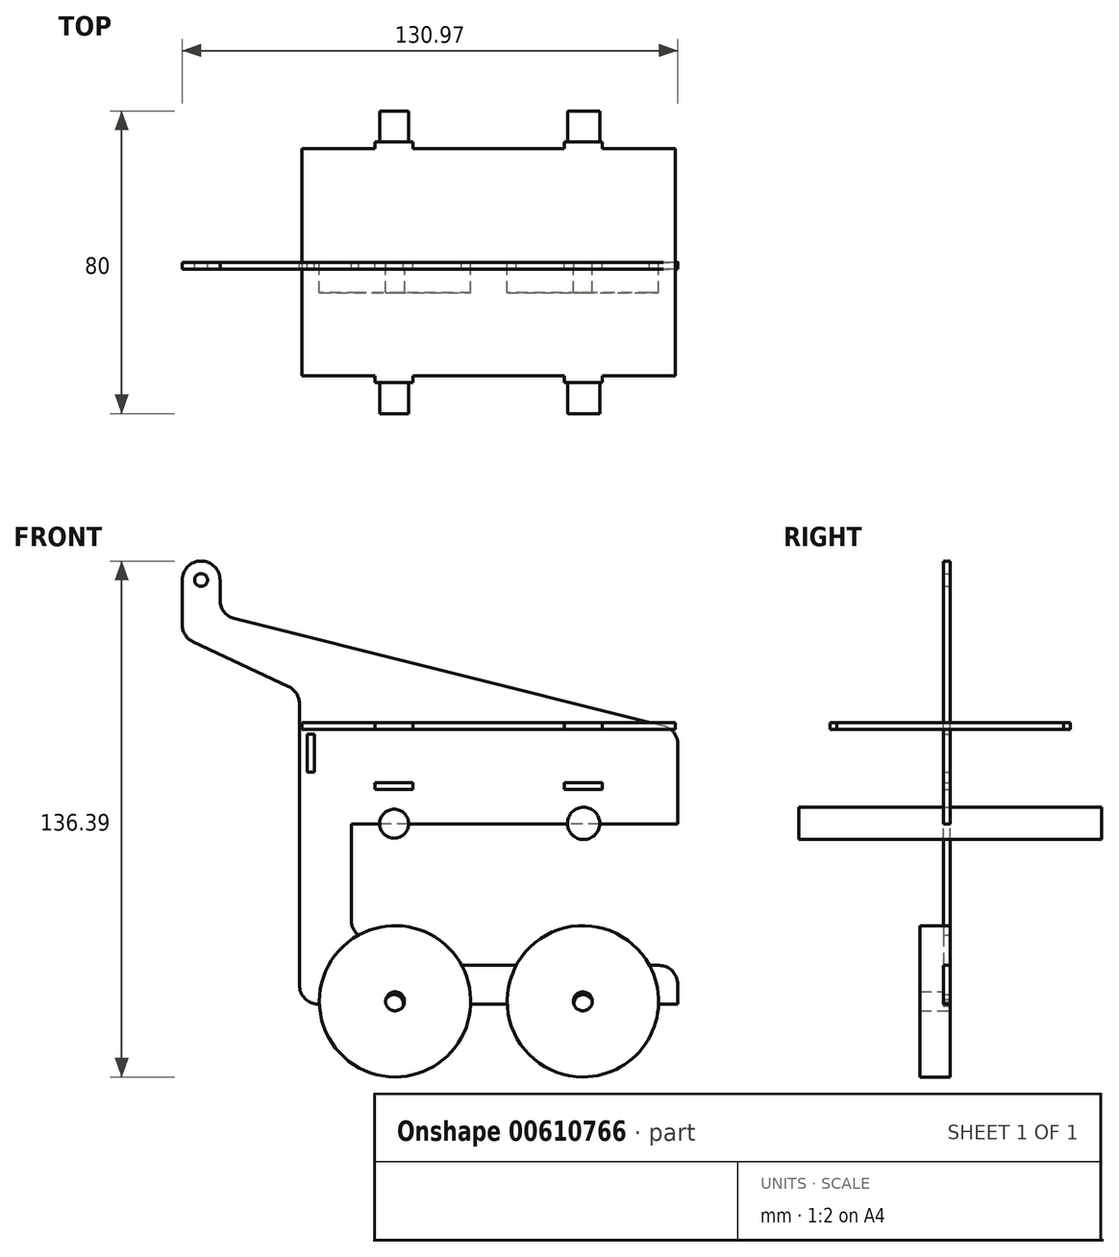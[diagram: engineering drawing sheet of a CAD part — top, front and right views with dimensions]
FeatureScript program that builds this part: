
annotation { "Feature Type Name" : "Feature", "Feature Type Description" : "" }
export const myFeature = defineFeature(function(context is Context, id is Id, definition is map)
    precondition{}
    {
        {
            var Q0;
            Q0=qCreatedBy(makeId("Front.planeOp"),FACE);
            var sketch = newSketch(context, id + "F0", { "sketchPlane" : qUnion([Q0])});
            skLineSegment(sketch, "E0.bottom", {"start": v(50, -25) * mm, "end": v(35, -25) * mm});
            skLineSegment(sketch, "E0.left", {"start": v(50, -25) * mm, "end": v(50, -3.9) * mm});
            skLineSegment(sketch, "E0.right", {"start": v(-50, -25) * mm, "end": v(-50, 6.83) * mm});
            skPoint(sketch, "E0.middle", {"position": v(0, 0) * mm});
            skLineSegment(sketch, "E1", {"start": v(35, -25) * mm, "end": v(50, -25) * mm, "construction": true});
            skLineSegment(sketch, "E2", {"start": v(46.21, 0.95) * mm, "end": v(-43.79, 23.45) * mm});
            skPoint(sketch, "E3.orphan", {"position": v(50, 25) * mm});
            skPoint(sketch, "E4.visualSharp", {"position": v(-50, 25) * mm});
            skPoint(sketch, "E5.visualSharp", {"position": v(50, 0) * mm});
            skArc(sketch, "E5.filletArc", {"start": v(50, -3.9) * mm, "mid": v(48.94, -0.83) * mm, "end": v(46.21, 0.95) * mm});
            skLineSegment(sketch, "E6", {"start": v(-50, -25) * mm, "end": v(-50, -15) * mm});
            skLineSegment(sketch, "E7", {"start": v(-50, -15) * mm, "end": v(50, -15) * mm, "construction": true});
            skLineSegment(sketch, "E8.bottom", {"start": v(-20, -15.9) * mm, "end": v(-30, -15.9) * mm});
            skLineSegment(sketch, "E8.top", {"start": v(-20, -14.1) * mm, "end": v(-30, -14.1) * mm});
            skLineSegment(sketch, "E8.left", {"start": v(-20, -15.9) * mm, "end": v(-20, -14.1) * mm});
            skLineSegment(sketch, "E8.right", {"start": v(-30, -15.9) * mm, "end": v(-30, -14.1) * mm});
            skPoint(sketch, "E8.middle", {"position": v(-25, -15) * mm});
            skLineSegment(sketch, "E9.bottom", {"start": v(30, -15.9) * mm, "end": v(20, -15.9) * mm});
            skLineSegment(sketch, "E9.top", {"start": v(30, -14.1) * mm, "end": v(20, -14.1) * mm});
            skLineSegment(sketch, "E9.left", {"start": v(30, -15.9) * mm, "end": v(30, -14.1) * mm});
            skLineSegment(sketch, "E9.right", {"start": v(20, -15.9) * mm, "end": v(20, -14.1) * mm});
            skPoint(sketch, "E9.middle", {"position": v(25, -15) * mm});
            skLineSegment(sketch, "E10", {"start": v(-43.79, 23.45) * mm, "end": v(-67.19, 29.3) * mm});
            skLineSegment(sketch, "E11", {"start": v(-70.97, 34.15) * mm, "end": v(-70.97, 39.5) * mm});
            skLineSegment(sketch, "E12", {"start": v(-75.97, 44.5) * mm, "end": v(-75.97, 44.5) * mm});
            skLineSegment(sketch, "E13", {"start": v(-80.97, 39.5) * mm, "end": v(-80.97, 27.68) * mm});
            skLineSegment(sketch, "E14", {"start": v(-78.1, 23.16) * mm, "end": v(-52.88, 11.36) * mm});
            skArc(sketch, "E15.filletArc", {"start": v(-50, 6.83) * mm, "mid": v(-50.78, 9.52) * mm, "end": v(-52.88, 11.36) * mm});
            skPoint(sketch, "E16.visualSharp", {"position": v(-80.97, 24.5) * mm});
            skArc(sketch, "E16.filletArc", {"start": v(-80.97, 27.68) * mm, "mid": v(-80.2, 25) * mm, "end": v(-78.1, 23.16) * mm});
            skPoint(sketch, "E17.visualSharp", {"position": v(-70.97, 30.24) * mm});
            skArc(sketch, "E17.filletArc", {"start": v(-70.97, 34.15) * mm, "mid": v(-69.91, 31.07) * mm, "end": v(-67.19, 29.3) * mm});
            skPoint(sketch, "E18.visualSharp", {"position": v(-70.97, 44.5) * mm});
            skArc(sketch, "E18.filletArc", {"start": v(-70.97, 39.5) * mm, "mid": v(-72.44, 43.04) * mm, "end": v(-75.97, 44.5) * mm});
            skPoint(sketch, "E19.visualSharp", {"position": v(-80.97, 44.5) * mm});
            skArc(sketch, "E19.filletArc", {"start": v(-75.97, 44.5) * mm, "mid": v(-79.5, 43.04) * mm, "end": v(-80.97, 39.5) * mm});
            skLineSegment(sketch, "E20", {"start": v(-47, -25) * mm, "end": v(-47, 12.38) * mm, "construction": true});
            skLineSegment(sketch, "E21.bottom", {"start": v(-46.1, -11.31) * mm, "end": v(-47.9, -11.31) * mm});
            skLineSegment(sketch, "E21.top", {"start": v(-46.1, -1.31) * mm, "end": v(-47.9, -1.31) * mm});
            skLineSegment(sketch, "E21.left", {"start": v(-46.1, -11.31) * mm, "end": v(-46.1, -1.31) * mm});
            skLineSegment(sketch, "E21.right", {"start": v(-47.9, -11.31) * mm, "end": v(-47.9, -1.31) * mm});
            skPoint(sketch, "E21.middle", {"position": v(-47, -6.31) * mm});
            skCircle(sketch, "E22", {"center": v(-75.97, 39.5) * mm, "radius": 1.7 * mm});
            skLineSegment(sketch, "E23", {"start": v(-50, -25) * mm, "end": v(-50, -67.61) * mm});
            skLineSegment(sketch, "E24", {"start": v(-45, -72.61) * mm, "end": v(-30, -72.61) * mm});
            skLineSegment(sketch, "E25", {"start": v(50, -72.61) * mm, "end": v(50, -67.4) * mm});
            skLineSegment(sketch, "E26", {"start": v(45, -62.4) * mm, "end": v(-22.16, -62.4) * mm});
            skLineSegment(sketch, "E27", {"start": v(-25.18, -61.38) * mm, "end": v(-34.28, -54.48) * mm});
            skLineSegment(sketch, "E28", {"start": v(-36.26, -50.5) * mm, "end": v(-36.26, -25) * mm});
            skPoint(sketch, "E29.visualSharp", {"position": v(-36.26, -52.98) * mm});
            skArc(sketch, "E29.filletArc", {"start": v(-36.26, -50.5) * mm, "mid": v(-35.74, -52.72) * mm, "end": v(-34.28, -54.48) * mm});
            skPoint(sketch, "E30.visualSharp", {"position": v(-23.84, -62.4) * mm});
            skArc(sketch, "E30.filletArc", {"start": v(-25.18, -61.38) * mm, "mid": v(-23.76, -62.14) * mm, "end": v(-22.16, -62.4) * mm});
            skPoint(sketch, "E31.visualSharp", {"position": v(-50, -72.61) * mm});
            skArc(sketch, "E31.filletArc", {"start": v(-50, -67.61) * mm, "mid": v(-48.54, -71.15) * mm, "end": v(-45, -72.61) * mm});
            skPoint(sketch, "E32.visualSharp", {"position": v(50, -62.4) * mm});
            skArc(sketch, "E32.filletArc", {"start": v(50, -67.4) * mm, "mid": v(48.54, -63.86) * mm, "end": v(45, -62.4) * mm});
            skCircle(sketch, "E33", {"center": v(-25, -72.61) * mm, "radius": 2.5 * mm});
            skCircle(sketch, "E34", {"center": v(25, -72.61) * mm, "radius": 2.5 * mm});
            skArc(sketch, "E35", {"start": v(-30, -72.61) * mm, "mid": v(-25, -77.61) * mm, "end": v(-20, -72.61) * mm});
            skArc(sketch, "E36", {"start": v(20, -72.61) * mm, "mid": v(25, -77.61) * mm, "end": v(30, -72.61) * mm});
            skLineSegment(sketch, "E37", {"start": v(-35, -25) * mm, "end": v(35, -25) * mm});
            skLineSegment(sketch, "E38", {"start": v(-35, -25) * mm, "end": v(-36.26, -25) * mm});
            skLineSegment(sketch, "E39.trimOffspring", {"start": v(-20, -72.61) * mm, "end": v(20, -72.61) * mm});
            skLineSegment(sketch, "E40.trimOffspring", {"start": v(30, -72.61) * mm, "end": v(50, -72.61) * mm});
            skSolve(sketch);
        }
        {
            var Q0;
            Q0=makeQuery(id+"F0.imprint","IMPRINT",FACE,{"disambiguationData":[TD([[makeQuery(id+"F0.imprint","IMPRINT",EDGE,{"derivedFrom":sQuery(id+"F0.wireOp",EDGE,"E0.bottom")}),-1.0]])]});
            extrude(context, id + "F1", {"entities" : qUnion([Q0]), "depth" : 1.8 * mm, "offsetDistance" : 25 * mm});
        }
        {
            var Q0;
            Q0=qCreatedBy(makeId("Front.planeOp"),FACE);
            var sketch = newSketch(context, id + "F2", { "sketchPlane" : qUnion([Q0])});
            skCircle(sketch, "E41", {"center": v(-24.96, -24.94) * mm, "radius": 3.83 * mm});
            skCircle(sketch, "E42", {"center": v(25.12, -24.84) * mm, "radius": 4.26 * mm});
            skSolve(sketch);
        }
        {
            var Q0;
            Q0 = qSketchRegion(id + "F2", true);
            extrude(context, id + "F3", {"entities" : qUnion([Q0]), "endBound" : BoundingType.SYMMETRIC, "depth" : 80 * mm, "offsetDistance" : 25 * mm});
        }
        {
            var Q0;
            Q0=qCreatedBy(makeId("Top.planeOp"),FACE);
            var sketch = newSketch(context, id + "F4", { "sketchPlane" : qUnion([Q0])});
            skLineSegment(sketch, "E43.bottom", {"start": v(-49.34, 30) * mm, "end": v(-30.02, 30) * mm});
            skLineSegment(sketch, "E43.top", {"start": v(-49.34, -30) * mm, "end": v(-30.02, -30) * mm});
            skLineSegment(sketch, "E43.left", {"start": v(-49.34, 30) * mm, "end": v(-49.34, -30) * mm});
            skLineSegment(sketch, "E43.right", {"start": v(49.34, 30) * mm, "end": v(49.34, -30) * mm});
            skPoint(sketch, "E43.middle", {"position": v(0, 0) * mm});
            skLineSegment(sketch, "E44.bottom", {"start": v(-20.02, 31.8) * mm, "end": v(-30.02, 31.8) * mm});
            skLineSegment(sketch, "E44.top", {"start": v(-20.02, -31.8) * mm, "end": v(-30.02, -31.8) * mm});
            skLineSegment(sketch, "E44.left", {"start": v(-20.02, 31.8) * mm, "end": v(-20.02, 30) * mm});
            skLineSegment(sketch, "E44.right", {"start": v(-30.02, 31.8) * mm, "end": v(-30.02, 30) * mm});
            skPoint(sketch, "E44.middle", {"position": v(-25.02, 0) * mm});
            skLineSegment(sketch, "E45.bottom", {"start": v(20, 31.8) * mm, "end": v(30, 31.8) * mm});
            skLineSegment(sketch, "E45.top", {"start": v(20, -31.8) * mm, "end": v(30, -31.8) * mm});
            skLineSegment(sketch, "E45.left", {"start": v(20, 31.8) * mm, "end": v(20, 30) * mm});
            skLineSegment(sketch, "E45.right", {"start": v(30, 31.8) * mm, "end": v(30, 30) * mm});
            skPoint(sketch, "E45.middle", {"position": v(25, 0) * mm});
            skLineSegment(sketch, "E46.trimOffspring", {"start": v(30, -30) * mm, "end": v(49.34, -30) * mm});
            skLineSegment(sketch, "E47.trimOffspring", {"start": v(-20.02, -30) * mm, "end": v(20, -30) * mm});
            skLineSegment(sketch, "E48.trimOffspring", {"start": v(-20.02, 30) * mm, "end": v(20, 30) * mm});
            skLineSegment(sketch, "E49.trimOffspring", {"start": v(30, 30) * mm, "end": v(49.34, 30) * mm});
            skLineSegment(sketch, "E50.trimOffspring", {"start": v(30, -30) * mm, "end": v(30, -31.8) * mm});
            skLineSegment(sketch, "E51.trimOffspring", {"start": v(20, -30) * mm, "end": v(20, -31.8) * mm});
            skLineSegment(sketch, "E52.trimOffspring", {"start": v(-20.02, -30) * mm, "end": v(-20.02, -31.8) * mm});
            skLineSegment(sketch, "E53.trimOffspring", {"start": v(-30.02, -30) * mm, "end": v(-30.02, -31.8) * mm});
            skSolve(sketch);
        }
        {
            var Q0;
            Q0=makeQuery(id+"F4.imprint","IMPRINT",FACE,{"disambiguationData":[TD([[makeQuery(id+"F4.imprint","IMPRINT",EDGE,{"derivedFrom":sQuery(id+"F4.wireOp",EDGE,"E43.bottom")}),-1.0]])]});
            extrude(context, id + "F5", {"entities" : qUnion([Q0]), "depth" : 1.8 * mm, "offsetDistance" : 25 * mm});
        }
        {
            var Q0;
            Q0=qCreatedBy(makeId("Front.planeOp"),FACE);
            var sketch = newSketch(context, id + "F6", { "sketchPlane" : qUnion([Q0])});
            skCircle(sketch, "E54", {"center": v(-24.72, -71.9) * mm, "radius": 2.5 * mm});
            skCircle(sketch, "E55", {"center": v(-24.72, -71.9) * mm, "radius": 20 * mm});
            skCircle(sketch, "E56", {"center": v(24.92, -71.9) * mm, "radius": 2.5 * mm});
            skCircle(sketch, "E57", {"center": v(24.92, -71.9) * mm, "radius": 20 * mm});
            skSolve(sketch);
        }
        {
            var Q0;
            Q0=makeQuery(id+"F6.imprint","IMPRINT",FACE,{"disambiguationData":[TD([[makeQuery(id+"F6.imprint","IMPRINT",EDGE,{"derivedFrom":sQuery(id+"F6.wireOp",EDGE,"E56")}),-1.0]])]});
            extrude(context, id + "F7", {"entities" : qUnion([Q0]), "operationType" : NewBodyOperationType.ADD, "depth" : 8 * mm, "offsetDistance" : 25 * mm});
        }
        {
            var Q0;
            Q0=makeQuery(id+"F6.imprint","IMPRINT",FACE,{"disambiguationData":[TD([[makeQuery(id+"F6.imprint","IMPRINT",EDGE,{"derivedFrom":sQuery(id+"F6.wireOp",EDGE,"E54")}),-1.0]])]});
            extrude(context, id + "F8", {"entities" : qUnion([Q0]), "operationType" : NewBodyOperationType.ADD, "depth" : 8 * mm, "offsetDistance" : 25 * mm});
        }
    });
